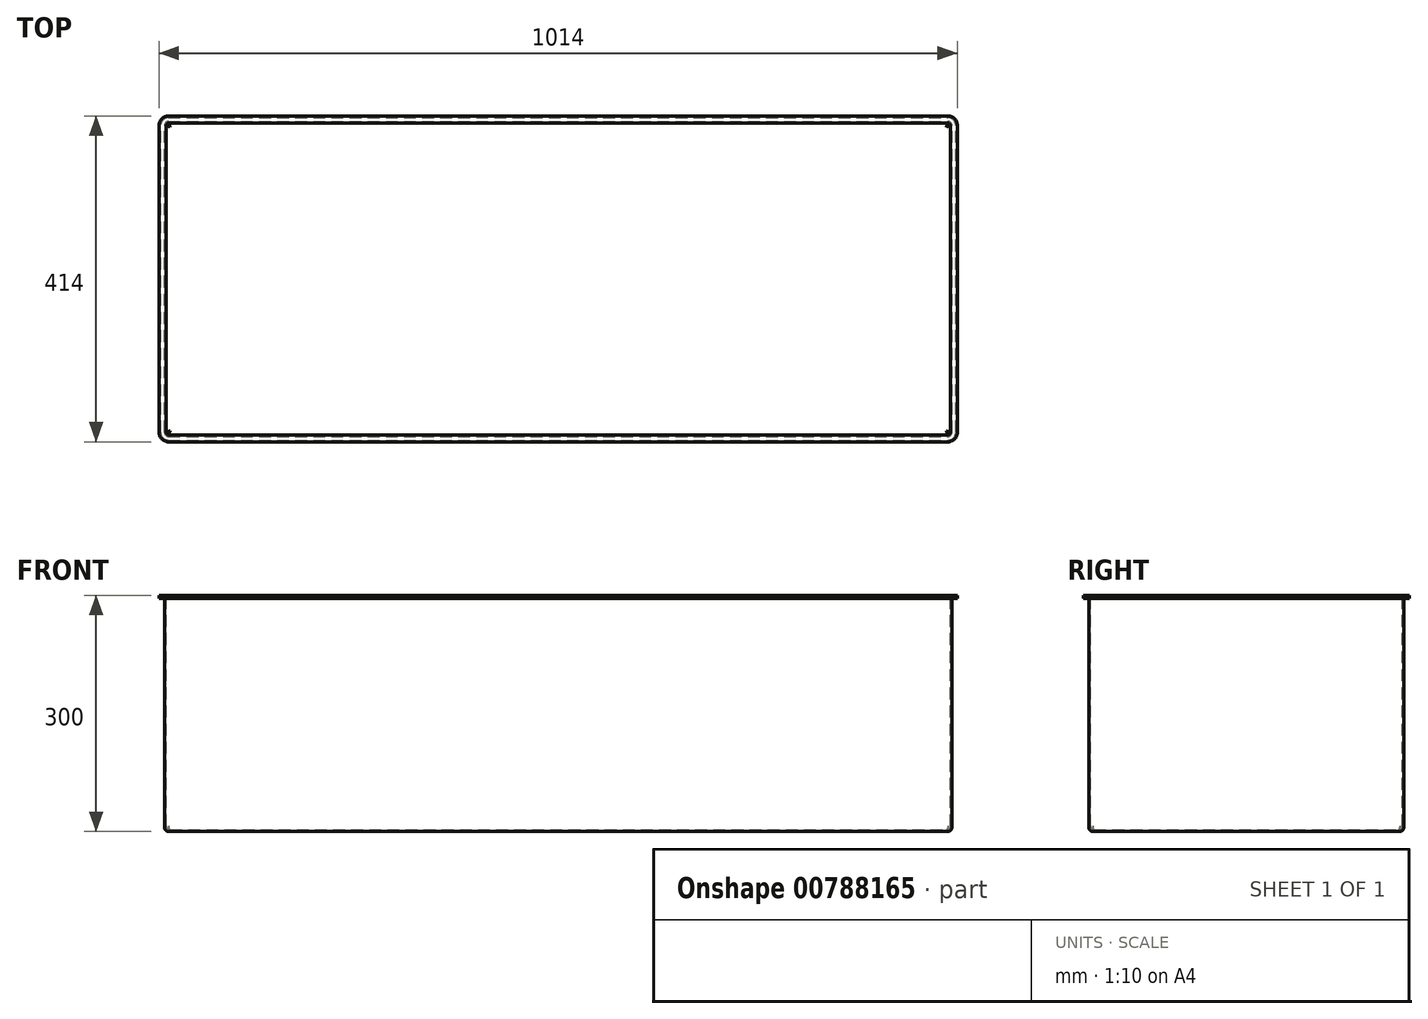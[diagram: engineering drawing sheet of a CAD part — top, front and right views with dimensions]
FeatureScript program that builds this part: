
annotation { "Feature Type Name" : "Feature", "Feature Type Description" : "" }
export const myFeature = defineFeature(function(context is Context, id is Id, definition is map)
    precondition{}
    {
        {
            var Q0;
            Q0=qCreatedBy(makeId("Top.planeOp"),FACE);
            var sketch = newSketch(context, id + "F0", { "sketchPlane" : qUnion([Q0])});
            skLineSegment(sketch, "E0.bottom", {"start": v(-500, -200) * mm, "end": v(500, -200) * mm});
            skLineSegment(sketch, "E0.top", {"start": v(-500, 200) * mm, "end": v(500, 200) * mm});
            skLineSegment(sketch, "E0.left", {"start": v(-500, -200) * mm, "end": v(-500, 200) * mm});
            skLineSegment(sketch, "E0.right", {"start": v(500, -200) * mm, "end": v(500, 200) * mm});
            skPoint(sketch, "E0.middle", {"position": v(0, 0) * mm});
            skSolve(sketch);
        }
        {
            var Q0;
            Q0=makeQuery(id+"F0.imprint","IMPRINT",FACE,{"disambiguationData":[TD([[makeQuery(id+"F0.imprint","IMPRINT",EDGE,{"derivedFrom":sQuery(id+"F0.wireOp",EDGE,"E0.bottom")}),1.0]])]});
            extrude(context, id + "F1", {"entities" : qUnion([Q0]), "depth" : 300 * mm, "offsetDistance" : 25 * mm});
        }
        {
            var Q0;
            Q0=makeQuery(id+"F5.opShell","OFFSET_FACE",FACE,{"disambiguationData":[OSD([sQuery(id+"F0.wireOp",EDGE,"E0.bottom"),sQuery(id+"F0.wireOp",EDGE,"E0.top"),sQuery(id+"F0.wireOp",EDGE,"E0.left"),sQuery(id+"F0.wireOp",EDGE,"E0.right")])]});
            var Q1;
            Q1=makeQuery(id+"F1.opExtrude","SWEPT_EDGE",EDGE,{"disambiguationData":[OSD([sQuery(id+"F0.wireOp",EDGE,"E0.bottom"),sQuery(id+"F0.wireOp",EDGE,"E0.right")])]});
            fillet(context, id + "F2", {"entities" : qUnion([Q0, Q1]), "radius" : 5 * mm, "tangentPropagation" : true, "allowEdgeOverflow" : false});
        }
        {
            var Q0;
            Q0=makeQuery(id+"F1.opExtrude","SWEPT_EDGE",EDGE,{"disambiguationData":[OSD([sQuery(id+"F0.wireOp",EDGE,"E0.top"),sQuery(id+"F0.wireOp",EDGE,"E0.right")])]});
            var Q1;
            Q1=makeQuery(id+"F1.opExtrude","SWEPT_EDGE",EDGE,{"disambiguationData":[OSD([sQuery(id+"F0.wireOp",EDGE,"E0.bottom"),sQuery(id+"F0.wireOp",EDGE,"E0.left")])]});
            fillet(context, id + "F3", {"entities" : qUnion([Q0, Q1]), "radius" : 5 * mm, "tangentPropagation" : true, "allowEdgeOverflow" : false});
        }
        {
            var Q0;
            Q0=makeQuery(id+"F1.opExtrude","SWEPT_EDGE",EDGE,{"disambiguationData":[OSD([sQuery(id+"F0.wireOp",EDGE,"E0.top"),sQuery(id+"F0.wireOp",EDGE,"E0.left")])]});
            fillet(context, id + "F4", {"entities" : qUnion([Q0]), "radius" : 5 * mm, "tangentPropagation" : true, "allowEdgeOverflow" : false});
        }
        {
            var Q0;
            Q0=makeQuery(id+"F1.opExtrude","CAP_FACE",FACE,{"disambiguationData":[OSD([sQuery(id+"F0.wireOp",EDGE,"E0.bottom"),sQuery(id+"F0.wireOp",EDGE,"E0.top"),sQuery(id+"F0.wireOp",EDGE,"E0.left"),sQuery(id+"F0.wireOp",EDGE,"E0.right")])],"isStart":false});
            shell(context, id + "F5", {"entities" : qUnion([Q0]), "thickness" : 2 * mm});
        }
        {
            var Q0;
            Q0=makeQuery(id+"F1.opExtrude","CAP_FACE",FACE,{"disambiguationData":[OSD([sQuery(id+"F0.wireOp",EDGE,"E0.bottom"),sQuery(id+"F0.wireOp",EDGE,"E0.top"),sQuery(id+"F0.wireOp",EDGE,"E0.left"),sQuery(id+"F0.wireOp",EDGE,"E0.right")])],"isStart":true});
            fillet(context, id + "F6", {"entities" : qUnion([Q0]), "radius" : 5 * mm, "tangentPropagation" : true, "allowEdgeOverflow" : false});
        }
        {
            var Q0;
            Q0=makeQuery(id+"F5.opShell","OFFSET_FACE",FACE,{"disambiguationData":[OSD([sQuery(id+"F0.wireOp",EDGE,"E0.bottom"),sQuery(id+"F0.wireOp",EDGE,"E0.top"),sQuery(id+"F0.wireOp",EDGE,"E0.left"),sQuery(id+"F0.wireOp",EDGE,"E0.right")])]});
            fillet(context, id + "F7", {"entities" : qUnion([Q0]), "radius" : 5 * mm, "tangentPropagation" : true, "allowEdgeOverflow" : false});
        }
        {
            var Q0;
            Q0=makeQuery(id+"F1.opExtrude","CAP_FACE",FACE,{"disambiguationData":[OSD([sQuery(id+"F0.wireOp",EDGE,"E0.bottom"),sQuery(id+"F0.wireOp",EDGE,"E0.top"),sQuery(id+"F0.wireOp",EDGE,"E0.left"),sQuery(id+"F0.wireOp",EDGE,"E0.right")])],"isStart":false});
            var sketch = newSketch(context, id + "F8", { "sketchPlane" : qUnion([Q0])});
            skArc(sketch, "E1.0", {"start": v(495, -205) * mm, "mid": v(502.07, -202.07) * mm, "end": v(505, -195) * mm});
            skLineSegment(sketch, "E1.1", {"start": v(-495, -205) * mm, "end": v(495, -205) * mm});
            skLineSegment(sketch, "E1.2", {"start": v(505, -195) * mm, "end": v(505, 195) * mm});
            skArc(sketch, "E1.3", {"start": v(-505, -195) * mm, "mid": v(-502.07, -202.07) * mm, "end": v(-495, -205) * mm});
            skArc(sketch, "E1.4", {"start": v(505, 195) * mm, "mid": v(502.07, 202.07) * mm, "end": v(495, 205) * mm});
            skLineSegment(sketch, "E1.5", {"start": v(-495, 205) * mm, "end": v(495, 205) * mm});
            skArc(sketch, "E1.6", {"start": v(-495, 205) * mm, "mid": v(-502.07, 202.07) * mm, "end": v(-505, 195) * mm});
            skLineSegment(sketch, "E1.7", {"start": v(-505, -195) * mm, "end": v(-505, 195) * mm});
            skSolve(sketch);
        }
        {
            var Q0;
            Q0=makeQuery(id+"F8.imprint","IMPRINT",FACE,{"disambiguationData":[TD([[makeQuery(id+"F8.imprint","IMPRINT",EDGE,{"derivedFrom":sQuery(id+"F8.wireOp",EDGE,"E1.0")}),1.0]])]});
            extrude(context, id + "F9", {"entities" : qUnion([Q0]), "operationType" : NewBodyOperationType.ADD, "depth" : -2 * mm, "offsetDistance" : 25 * mm});
        }
        {
            var Q0;
            {var subQ0=sQuery(id+"F0.wireOp",EDGE,"E0.right");var subQ1=sQuery(id+"F0.wireOp",EDGE,"E0.left");var subQ2=sQuery(id+"F0.wireOp",EDGE,"E0.top");var subQ3=sQuery(id+"F0.wireOp",EDGE,"E0.bottom");Q0=makeQuery(id+"F9.boolean.opBoolean","MERGE",FACE,{"derivedFrom":[makeQuery(id+"F1.opExtrude","CAP_FACE",FACE,{"disambiguationData":[OSD([subQ3,subQ2,subQ1,subQ0])],"isStart":false}),makeQuery(id+"F9.opExtrude","CAP_FACE",FACE,{"disambiguationData":[OSD([subQ3,subQ2,subQ1,subQ0,sQuery(id+"F8.wireOp",EDGE,"E1.0"),sQuery(id+"F8.wireOp",EDGE,"E1.1"),sQuery(id+"F8.wireOp",EDGE,"E1.2"),sQuery(id+"F8.wireOp",EDGE,"E1.3"),sQuery(id+"F8.wireOp",EDGE,"E1.4"),sQuery(id+"F8.wireOp",EDGE,"E1.5"),sQuery(id+"F8.wireOp",EDGE,"E1.6"),sQuery(id+"F8.wireOp",EDGE,"E1.7")])],"isStart":true})]});}
            var sketch = newSketch(context, id + "F10", { "sketchPlane" : qUnion([Q0])});
            skArc(sketch, "E2.0", {"start": v(-495, 207) * mm, "mid": v(-503.49, 203.49) * mm, "end": v(-507, 195) * mm});
            skLineSegment(sketch, "E2.1", {"start": v(-507, -195) * mm, "end": v(-507, 195) * mm});
            skLineSegment(sketch, "E2.2", {"start": v(-495, 207) * mm, "end": v(495, 207) * mm});
            skArc(sketch, "E2.3", {"start": v(-507, -195) * mm, "mid": v(-503.49, -203.49) * mm, "end": v(-495, -207) * mm});
            skArc(sketch, "E2.4", {"start": v(507, 195) * mm, "mid": v(503.49, 203.49) * mm, "end": v(495, 207) * mm});
            skLineSegment(sketch, "E2.5", {"start": v(507, -195) * mm, "end": v(507, 195) * mm});
            skArc(sketch, "E2.6", {"start": v(495, -207) * mm, "mid": v(503.49, -203.49) * mm, "end": v(507, -195) * mm});
            skLineSegment(sketch, "E2.7", {"start": v(-495, -207) * mm, "end": v(495, -207) * mm});
            skSolve(sketch);
        }
        {
            var Q0;
            Q0=makeQuery(id+"F10.imprint","IMPRINT",FACE,{"disambiguationData":[TD([[makeQuery(id+"F10.imprint","IMPRINT",EDGE,{"derivedFrom":sQuery(id+"F10.wireOp",EDGE,"E2.0")}),1.0]])]});
            extrude(context, id + "F11", {"entities" : qUnion([Q0]), "operationType" : NewBodyOperationType.ADD, "depth" : -4 * mm, "offsetDistance" : 25 * mm});
        }
        {
            var Q0;
            Q0=makeQuery(id+"F1.opExtrude","SWEPT_BODY",BODY,{"disambiguationData":[OSD([sQuery(id+"F0.wireOp",EDGE,"E0.bottom"),sQuery(id+"F0.wireOp",EDGE,"E0.top"),sQuery(id+"F0.wireOp",EDGE,"E0.left"),sQuery(id+"F0.wireOp",EDGE,"E0.right")])]});
            transform(context, id + "F12", {"entities" : qUnion([Q0]), "transformType" : TransformType.TRANSLATION_3D, "dx" : 0 * mm, "dy" : 0 * mm, "dz" : 0 * mm, "makeCopy" : true});
        }
        {
            var Q0;
            Q0=makeQuery(id+"F12.opPattern","COPY",BODY,{"derivedFrom":makeQuery(id+"F1.opExtrude","SWEPT_BODY",BODY,{"disambiguationData":[OSD([sQuery(id+"F0.wireOp",EDGE,"E0.bottom"),sQuery(id+"F0.wireOp",EDGE,"E0.top"),sQuery(id+"F0.wireOp",EDGE,"E0.left"),sQuery(id+"F0.wireOp",EDGE,"E0.right")])]}),"instanceName":"1"});
            deleteBodies(context, id + "F13", {"entities" : qUnion([Q0])});
        }
    });
